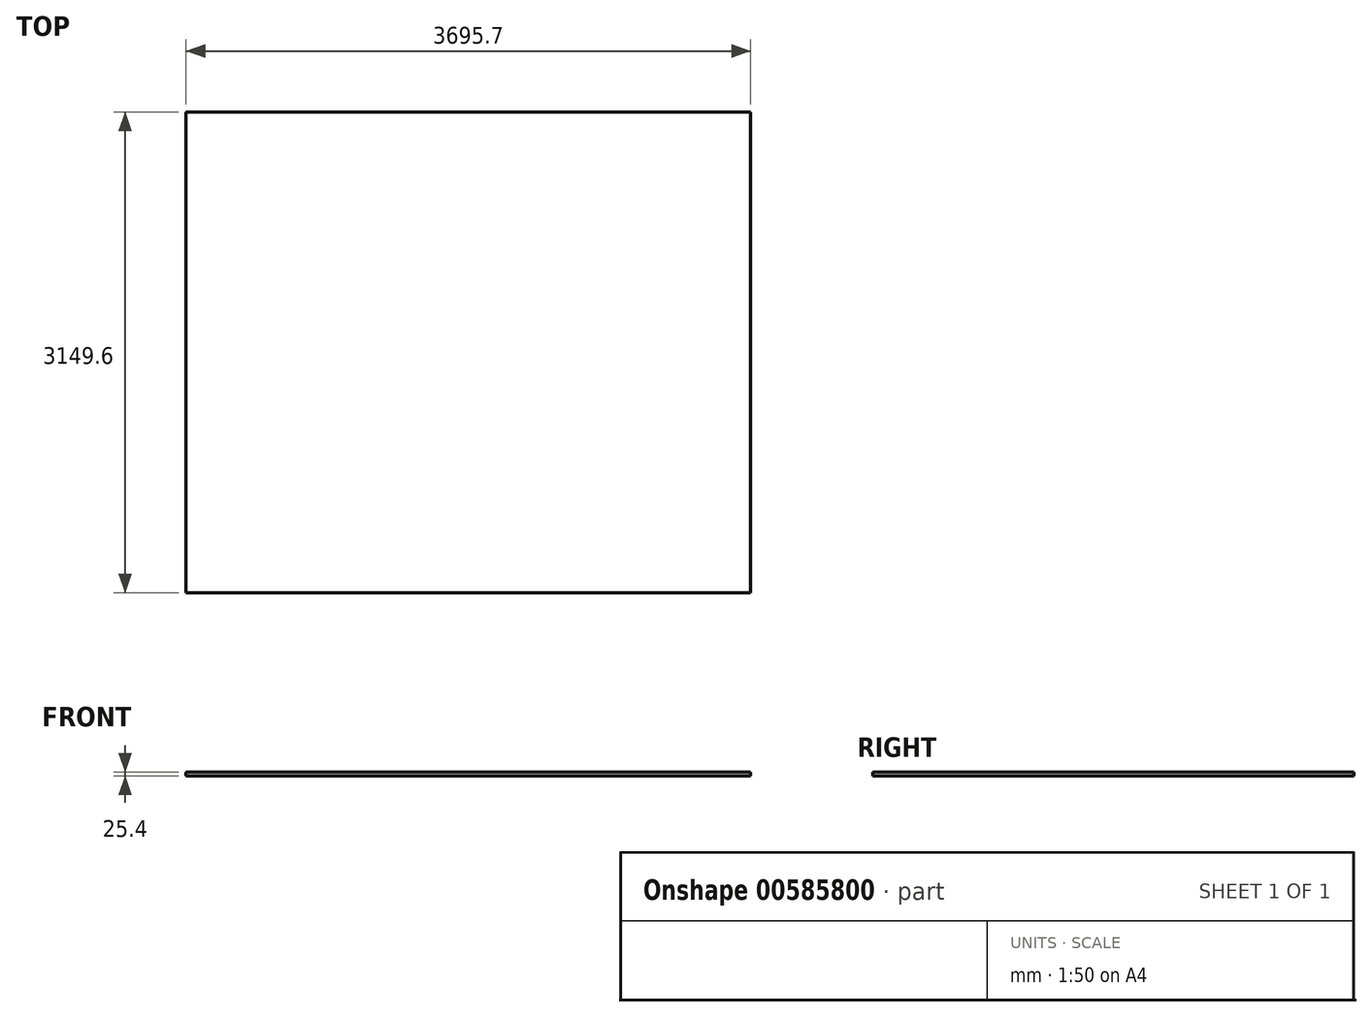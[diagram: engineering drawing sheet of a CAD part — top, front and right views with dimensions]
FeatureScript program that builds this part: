
annotation { "Feature Type Name" : "Feature", "Feature Type Description" : "" }
export const myFeature = defineFeature(function(context is Context, id is Id, definition is map)
    precondition{}
    {
        {
            var Q0;
            Q0=qCreatedBy(makeId("Top.planeOp"),FACE);
            var sketch = newSketch(context, id + "F0", { "sketchPlane" : qUnion([Q0])});
            skLineSegment(sketch, "E0.bottom", {"start": v(1847.85, -1574.8) * mm, "end": v(-1847.85, -1574.8) * mm});
            skLineSegment(sketch, "E0.top", {"start": v(1847.85, 1574.8) * mm, "end": v(-1847.85, 1574.8) * mm});
            skLineSegment(sketch, "E0.left", {"start": v(1847.85, -1574.8) * mm, "end": v(1847.85, 1574.8) * mm});
            skLineSegment(sketch, "E0.right", {"start": v(-1847.85, -1574.8) * mm, "end": v(-1847.85, 1574.8) * mm});
            skPoint(sketch, "E0.middle", {"position": v(0, 0) * mm});
            skSolve(sketch);
        }
        {
            var Q0;
            Q0 = qSketchRegion(id + "F0", true);
            extrude(context, id + "F1", {"entities" : qUnion([Q0]), "oppositeDirection" : true, "depth" : 25.4 * mm, "offsetDistance" : 25.4 * mm});
        }
        {
            var Q0;
            Q0=makeQuery(id+"F1.opExtrude","CAP_FACE",FACE,{"disambiguationData":[OSD([sQuery(id+"F0.wireOp",EDGE,"E0.bottom"),sQuery(id+"F0.wireOp",EDGE,"E0.top"),sQuery(id+"F0.wireOp",EDGE,"E0.left"),sQuery(id+"F0.wireOp",EDGE,"E0.right")])],"isStart":true});
            cPlane(context, id + "F2", {"entities" : qUnion([Q0]), "cplaneType" : CPlaneType.OFFSET, "offset" : 95.25 * mm, "width" : 152.4 * mm, "height" : 152.4 * mm});
        }
    });
